FCSTD DOCUMENT  (FreeCAD 0.17R13541 (Git))
Label: Xtrusion4mmx5
License: All rights reserved
LicenseURL: http://en.wikipedia.org/wiki/All_rights_reserved
objects: Sketcher::SketchObject×1
note: 1 computed .brp shape members not serialized (recipe doc carries the construction recipe); baked Part::Feature solids carry a one-line shape summary decoded from their .brp

FEATURE [Sketcher::SketchObject] Sketch
  sketch-geometry (28):
    g0: LineSegment StartX=-73.5421 StartY=-24.5421 StartZ=0 EndX=-60.771 EndY=-24.5421 EndZ=0
    g1: LineSegment StartX=-60.771 StartY=-24.5421 StartZ=0 EndX=-65.771 EndY=-19.5421 EndZ=0
    g2: LineSegment StartX=-65.771 StartY=-19.5421 StartZ=0 EndX=-51.771 EndY=-19.5421 EndZ=0
    g3: LineSegment StartX=-51.771 StartY=-19.5421 StartZ=0 EndX=-56.771 EndY=-24.5421 EndZ=0
    g4: LineSegment StartX=-56.771 StartY=-24.5421 StartZ=0 EndX=-44 EndY=-24.5421 EndZ=0
    g5: LineSegment StartX=-44 StartY=-24.5421 StartZ=0 EndX=-44 EndY=-11.7711 EndZ=0
    g6: LineSegment StartX=-44 StartY=-11.7711 StartZ=0 EndX=-49 EndY=-16.7711 EndZ=0
    g7: LineSegment StartX=-49 StartY=-16.7711 StartZ=0 EndX=-49 EndY=-2.77105 EndZ=0
    g8: LineSegment StartX=-49 StartY=-2.77105 StartZ=0 EndX=-44 EndY=-7.77105 EndZ=0
    g9: LineSegment StartX=-44 StartY=-7.77105 StartZ=0 EndX=-44 EndY=5 EndZ=0
    g10: LineSegment StartX=-44 StartY=5 StartZ=0 EndX=-56.771 EndY=5 EndZ=0
    g11: LineSegment StartX=-56.771 StartY=5 StartZ=0 EndX=-51.771 EndY=0 EndZ=0
    g12: LineSegment StartX=-51.771 StartY=0 StartZ=0 EndX=-65.771 EndY=0 EndZ=0
    g13: LineSegment StartX=-65.771 StartY=0 StartZ=0 EndX=-60.771 EndY=5 EndZ=0
    g14: LineSegment StartX=-60.771 StartY=5 StartZ=0 EndX=-73.5421 EndY=5 EndZ=0
    g15: LineSegment StartX=-73.5421 StartY=5 StartZ=0 EndX=-73.5421 EndY=-7.77105 EndZ=0
    g16: LineSegment StartX=-73.5421 StartY=-7.77105 StartZ=0 EndX=-68.5421 EndY=-2.77105 EndZ=0
    g17: LineSegment StartX=-68.5421 StartY=-2.77105 StartZ=0 EndX=-68.5421 EndY=-16.7711 EndZ=0
    g18: LineSegment StartX=-68.5421 StartY=-16.7711 StartZ=0 EndX=-73.5421 EndY=-11.7711 EndZ=0
    g19: LineSegment StartX=-73.5421 StartY=-11.7711 StartZ=0 EndX=-73.5421 EndY=-24.5421 EndZ=0
    g20: LineSegment [constr] StartX=-60.771 StartY=-24.5421 StartZ=0 EndX=-56.771 EndY=-24.5421 EndZ=0
    g21: LineSegment [constr] StartX=-60.771 StartY=5 StartZ=0 EndX=-56.771 EndY=5 EndZ=0
    g22: LineSegment [constr] StartX=-44 StartY=-7.77105 StartZ=0 EndX=-44 EndY=-11.7711 EndZ=0
    g23: LineSegment [constr] StartX=-73.5421 StartY=-7.77105 StartZ=0 EndX=-73.5421 EndY=-11.7711 EndZ=0
    g24: LineSegment [constr] StartX=-65.771 StartY=-19.5421 StartZ=0 EndX=-65.771 EndY=-24.5421 EndZ=0
    g25: LineSegment [constr] StartX=-68.5421 StartY=-16.7711 StartZ=0 EndX=-73.5421 EndY=-16.7711 EndZ=0
    g26: LineSegment [constr] StartX=-65.771 StartY=5 StartZ=0 EndX=-65.771 EndY=0 EndZ=0
    g27: LineSegment [constr] StartX=-49 StartY=-2.77105 StartZ=0 EndX=-44 EndY=-2.77105 EndZ=0
  constraints (82):
    c: Horizontal(g0)
    c: Coincident(g0,g1)
    c: Coincident(g1,g2)
    c: Horizontal(g2)
    c: Coincident(g2,g3)
    c: Coincident(g3,g4)
    c: Horizontal(g4)
    c: Coincident(g4,g5)
    c: Vertical(g5)
    c: Coincident(g5,g6)
    c: Coincident(g6,g7)
    c: Vertical(g7)
    c: Coincident(g7,g8)
    c: Coincident(g8,g9)
    c: Vertical(g9)
    c: Coincident(g9,g10)
    c: Horizontal(g10)
    c: Coincident(g10,g11)
    c: Coincident(g11,g12)
    c: PointOnObject(g12,g-1)
    c: Horizontal(g12)
    c: Coincident(g12,g13)
    c: Coincident(g13,g14)
    c: Horizontal(g14)
    c: Coincident(g14,g15)
    c: Vertical(g15)
    c: Coincident(g15,g16)
    c: Coincident(g16,g17)
    c: Vertical(g17)
    c: Coincident(g17,g18)
    c: Coincident(g18,g19)
    c: Vertical(g19)
    c: Equal(g14,g10)
    c: Equal(g10,g9)
    c: Equal(g9,g5)
    c: Equal(g5,g4)
    c: Equal(g4,g0)
    c: Equal(g0,g19)
    c: Equal(g19,g15)
    c: Equal(g17,g12)
    c: Equal(g12,g7)
    c: Equal(g7,g2)
    c: Angle(g1,g0) = 0.785398
    c: Angle(g19,g18) = 0.785398
    c: Angle(g4,g3) = 0.785398
    c: Angle(g6,g5) = 0.785398
    c: Angle(g9,g8) = 0.785398
    c: Angle(g11,g10) = 0.785398
    c: Angle(g14,g13) = 0.785398
    c: Angle(g16,g15) = 0.785398
    c: Equal(g16,g13)
    c: Equal(g13,g11)
    c: Equal(g11,g8)
    c: Equal(g8,g6)
    c: Equal(g6,g3)
    c: Equal(g3,g1)
    c: Equal(g1,g18)
    c: Coincident(g20,g0)
    c: Coincident(g20,g3)
    c: Coincident(g21,g13)
    c: Coincident(g21,g10)
    c: Coincident(g22,g8)
    c: Coincident(g22,g5)
    c: Coincident(g23,g15)
    c: Coincident(g23,g18)
    c: Equal(g23,g21)
    c: Equal(g21,g22)
    c: Equal(g22,g20)
    c: Distance(g21) = 4
    c: Coincident(g24,g1)
    c: PointOnObject(g24,g0)
    c: Vertical(g24)
    c: Coincident(g25,g17)
    c: PointOnObject(g25,g19)
    c: Horizontal(g25)
    c: PointOnObject(g26,g14)
    c: Coincident(g26,g12)
    c: Coincident(g27,g7)
    c: Horizontal(g27)
    c: Equal(g27,g26)
    c: Equal(g26,g25)
    c: Distance(g26) = 5
